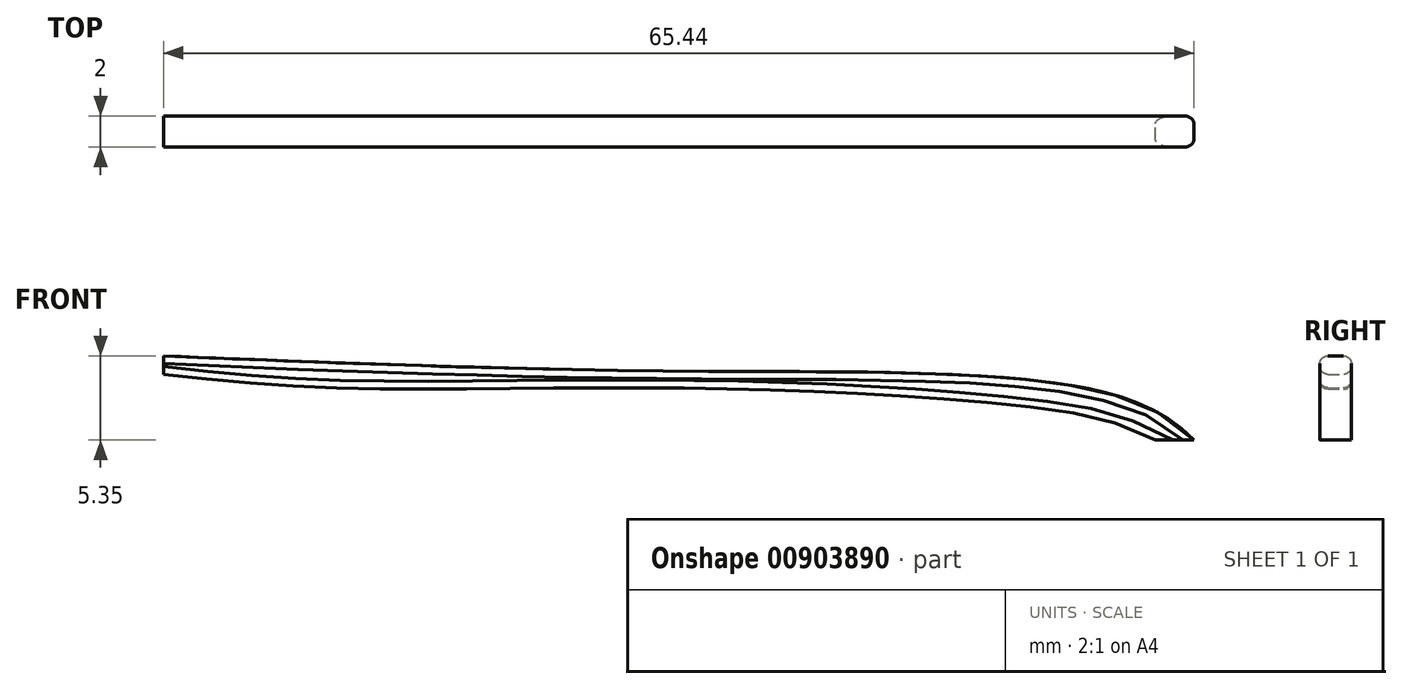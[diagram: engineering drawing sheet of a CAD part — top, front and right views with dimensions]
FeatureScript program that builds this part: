
annotation { "Feature Type Name" : "Feature", "Feature Type Description" : "" }
export const myFeature = defineFeature(function(context is Context, id is Id, definition is map)
    precondition{}
    {
        {
            var Q0;
            Q0=qCreatedBy(makeId("Front.planeOp"),FACE);
            var sketch = newSketch(context, id + "F0", { "sketchPlane" : qUnion([Q0])});
            skFitSpline(sketch, "E0", {"points": [v(16.8, 0) * mm, v(10, 3.29) * mm, v(-14.89, 4.38) * mm, v(-48.64, 5.35) * mm], "startDerivative": vector(-20.68, 22.93) * mm, "endDerivative": vector(-77.41, 3.38) * mm});
            skFitSpline(sketch, "E1", {"points": [v(14.34, 0) * mm, v(10, 1.55) * mm, v(-14.44, 3.29) * mm, v(-37.24, 3.29) * mm, v(-48.64, 4.17) * mm], "startDerivative": vector(-28.8, 14.21) * mm, "endDerivative": vector(-46.75, 5.4) * mm});
            skLineSegment(sketch, "E2", {"start": v(-48.64, 5.35) * mm, "end": v(-48.64, 4.17) * mm});
            skLineSegment(sketch, "E3", {"start": v(16.8, 0) * mm, "end": v(14.34, 0) * mm});
            skSolve(sketch);
        }
        {
            var Q0;
            Q0 = qSketchRegion(id + "F0", true);
            extrude(context, id + "F1", {"entities" : qUnion([Q0]), "depth" : 2 * mm, "offsetDistance" : 25 * mm});
        }
        {
            var Q0;
            Q0=makeQuery(id+"F1.opExtrude","CAP_EDGE",EDGE,{"disambiguationData":[OSD([sQuery(id+"F0.wireOp",EDGE,"E0")])],"isStart":true});
            var Q1;
            Q1=makeQuery(id+"F1.opExtrude","CAP_EDGE",EDGE,{"disambiguationData":[OSD([sQuery(id+"F0.wireOp",EDGE,"E0")])],"isStart":false});
            var Q2;
            Q2=makeQuery(id+"F1.opExtrude","CAP_EDGE",EDGE,{"disambiguationData":[OSD([sQuery(id+"F0.wireOp",EDGE,"E1")])],"isStart":true});
            var Q3;
            Q3=makeQuery(id+"F1.opExtrude","CAP_EDGE",EDGE,{"disambiguationData":[OSD([sQuery(id+"F0.wireOp",EDGE,"E1")])],"isStart":false});
            fillet(context, id + "F2", {"entities" : qUnion([Q0, Q1, Q2, Q3]), "radius" : 0.5 * mm, "tangentPropagation" : true, "allowEdgeOverflow" : false});
        }
    });
